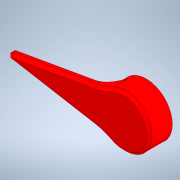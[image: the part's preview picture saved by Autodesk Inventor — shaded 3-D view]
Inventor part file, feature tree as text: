
AUTODESK INVENTOR PART (.ipt)
format: ipt  version: 2021.2 (Build 252289000, 289)  size: 159,744 bytes
history: native  units: mm
features: extrude x3, other x1, sketch x1, fillet x1, chamfer x1
ambient origin geometry x8: Origin, YZ Plane, XZ Plane, XY Plane, X Axis, Y Axis, Z Axis, Center Point
bodies: Body1 (feature_tree)
feature tree (7):
  other  "Твердое тело1"
  sketch  "Эскиз1"
  extrude  "Выдавливание1"  Depth=6.7mm
  extrude  "Выдавливание3"  Depth=1.2mm
  extrude  "Выдавливание4"  Depth=40.0mm
  fillet  "Сопряжение1"  Radius=0.5mm
  chamfer  "Фаска1"  Distance=3.490659mm
